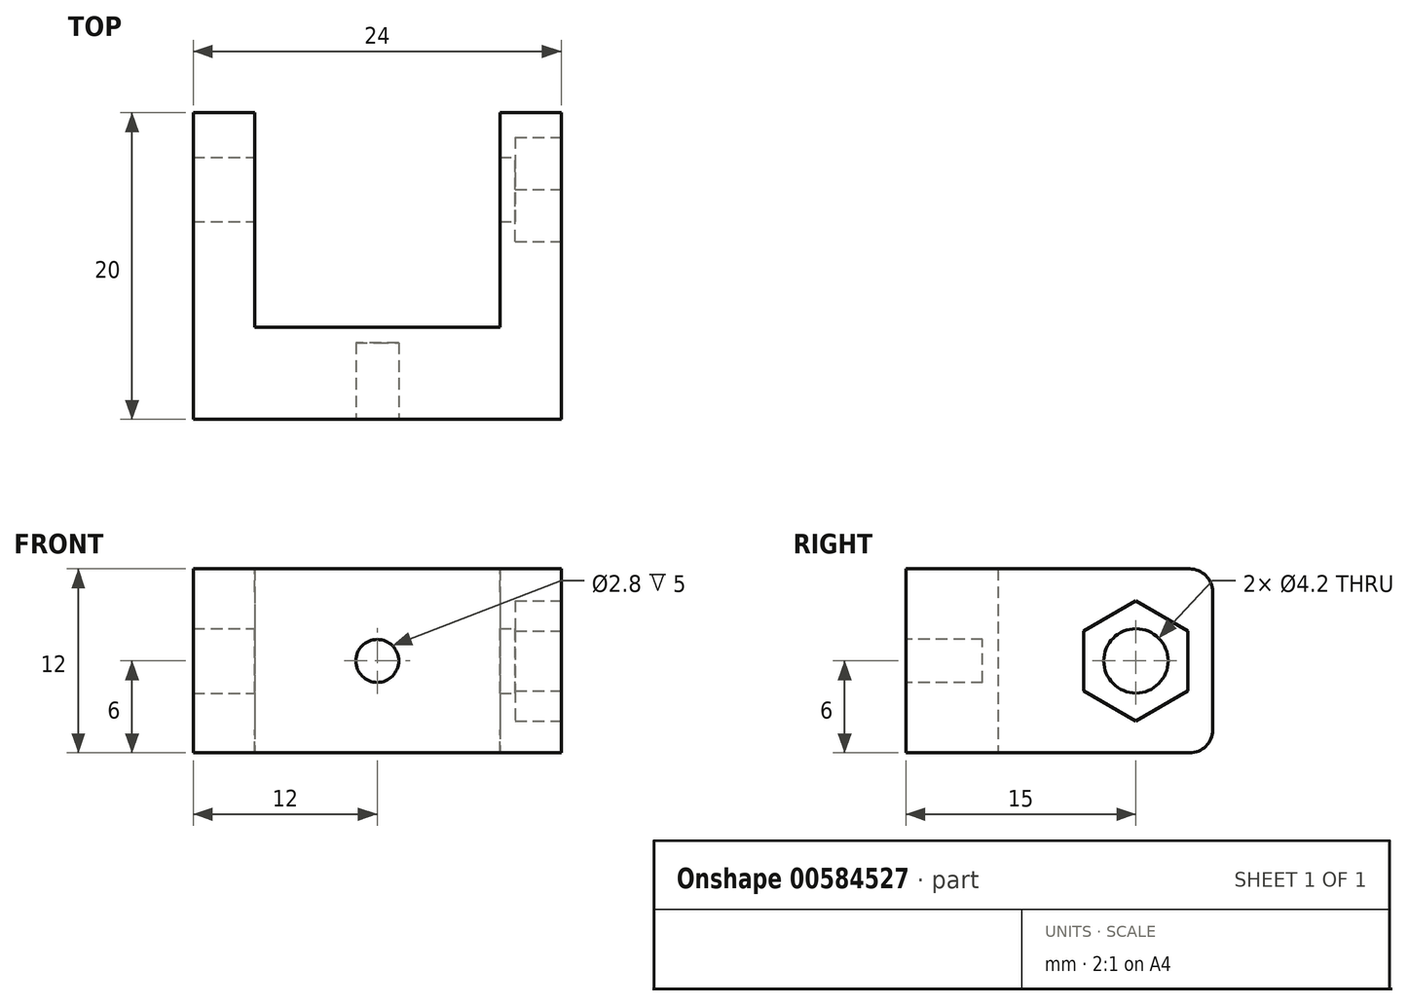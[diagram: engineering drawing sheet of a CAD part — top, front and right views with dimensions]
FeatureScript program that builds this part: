
annotation { "Feature Type Name" : "Feature", "Feature Type Description" : "" }
export const myFeature = defineFeature(function(context is Context, id is Id, definition is map)
    precondition{}
    {
        {
            var Q0;
            Q0=qCreatedBy(makeId("Top.planeOp"),FACE);
            var sketch = newSketch(context, id + "F0", { "sketchPlane" : qUnion([Q0])});
            skLineSegment(sketch, "E0.bottom", {"start": v(12, 10) * mm, "end": v(8, 10) * mm});
            skLineSegment(sketch, "E0.top", {"start": v(12, -10) * mm, "end": v(-12, -10) * mm});
            skLineSegment(sketch, "E0.left", {"start": v(12, 10) * mm, "end": v(12, -10) * mm});
            skLineSegment(sketch, "E0.right", {"start": v(-12, 10) * mm, "end": v(-12, -10) * mm});
            skPoint(sketch, "E0.middle", {"position": v(0, 0) * mm});
            skLineSegment(sketch, "E1", {"start": v(-8, 10) * mm, "end": v(-8, -4) * mm});
            skLineSegment(sketch, "E2", {"start": v(-8, -4) * mm, "end": v(0, -4) * mm});
            skLineSegment(sketch, "E3.MirrorCS", {"start": v(8, 10) * mm, "end": v(8, -4) * mm});
            skLineSegment(sketch, "E4.MirrorCS", {"start": v(8, -4) * mm, "end": v(0, -4) * mm});
            skLineSegment(sketch, "E5.trimOffspring", {"start": v(-8, 10) * mm, "end": v(-12, 10) * mm});
            skSolve(sketch);
        }
        {
            var Q0;
            Q0 = qSketchRegion(id + "F0", true);
            extrude(context, id + "F1", {"entities" : qUnion([Q0]), "endBound" : BoundingType.SYMMETRIC, "depth" : 12 * mm, "offsetDistance" : 25 * mm});
        }
        {
            var Q0;
            Q0=qCreatedBy(makeId("Right.planeOp"),FACE);
            var sketch = newSketch(context, id + "F2", { "sketchPlane" : qUnion([Q0])});
            skLineSegment(sketch, "E6", {"start": v(0, 0) * mm, "end": v(17.34, 0) * mm, "construction": true});
            skCircle(sketch, "E7", {"center": v(5, 0) * mm, "radius": 2.1 * mm});
            skSolve(sketch);
        }
        {
            var Q0;
            Q0 = qSketchRegion(id + "F2", true);
            extrude(context, id + "F3", {"entities" : qUnion([Q0]), "operationType" : NewBodyOperationType.REMOVE, "endBound" : BoundingType.SYMMETRIC, "oppositeDirection" : true, "depth" : 50 * mm, "offsetDistance" : 25 * mm});
        }
        {
            var Q0;
            Q0=makeQuery(id+"F1.opExtrude","SWEPT_FACE",FACE,{"disambiguationData":[OSD([sQuery(id+"F0.wireOp",EDGE,"E0.left")])]});
            cPlane(context, id + "F4", {"entities" : qUnion([Q0]), "cplaneType" : CPlaneType.OFFSET, "offset" : 0 * mm, "width" : 150 * mm, "height" : 150 * mm});
        }
        {
            var Q0;
            Q0=qCreatedBy(id+"F4.planeOp",FACE);
            var sketch = newSketch(context, id + "F5", { "sketchPlane" : qUnion([Q0])});
            skCircle(sketch, "E8.cCircle", {"center": v(5, 0) * mm, "radius": 3.4 * mm, "construction": true});
            skLineSegment(sketch, "E8.0", {"start": v(8.4, -1.96) * mm, "end": v(5, -3.93) * mm});
            skLineSegment(sketch, "E8.1", {"start": v(5, -3.93) * mm, "end": v(1.6, -1.96) * mm});
            skLineSegment(sketch, "E8.2", {"start": v(1.6, -1.96) * mm, "end": v(1.6, 1.96) * mm});
            skLineSegment(sketch, "E8.3", {"start": v(1.6, 1.96) * mm, "end": v(5, 3.93) * mm});
            skLineSegment(sketch, "E8.4", {"start": v(5, 3.93) * mm, "end": v(8.4, 1.96) * mm});
            skLineSegment(sketch, "E8.5", {"start": v(8.4, 1.96) * mm, "end": v(8.4, -1.96) * mm});
            skPoint(sketch, "E8.0.midPoint", {"position": v(6.7, -2.94) * mm});
            skSolve(sketch);
        }
        {
            var Q0;
            Q0 = qSketchRegion(id + "F5", true);
            extrude(context, id + "F6", {"entities" : qUnion([Q0]), "operationType" : NewBodyOperationType.REMOVE, "oppositeDirection" : true, "depth" : 3 * mm, "offsetDistance" : 25 * mm});
        }
        {
            var Q0;
            Q0=makeQuery(id+"F1.opExtrude","CAP_EDGE",EDGE,{"disambiguationData":[OSD([sQuery(id+"F0.wireOp",EDGE,"E0.bottom")])],"isStart":true});
            var Q1;
            Q1=makeQuery(id+"F1.opExtrude","CAP_EDGE",EDGE,{"disambiguationData":[OSD([sQuery(id+"F0.wireOp",EDGE,"E0.bottom")])],"isStart":false});
            var Q2;
            Q2=makeQuery(id+"F1.opExtrude","CAP_EDGE",EDGE,{"disambiguationData":[OSD([sQuery(id+"F0.wireOp",EDGE,"E5.trimOffspring")])],"isStart":true});
            var Q3;
            Q3=makeQuery(id+"F1.opExtrude","CAP_EDGE",EDGE,{"disambiguationData":[OSD([sQuery(id+"F0.wireOp",EDGE,"E5.trimOffspring")])],"isStart":false});
            fillet(context, id + "F7", {"entities" : qUnion([Q0, Q1, Q2, Q3]), "tangentPropagation" : true, "radius" : 1.5 * mm, "defaultsChanged" : true, "vertexSettings" : [], "allowEdgeOverflow" : false});
        }
        {
            var Q0;
            Q0=makeQuery(id+"F1.opExtrude","SWEPT_FACE",FACE,{"disambiguationData":[OSD([sQuery(id+"F0.wireOp",EDGE,"E0.top")])]});
            cPlane(context, id + "F8", {"entities" : qUnion([Q0]), "cplaneType" : CPlaneType.OFFSET, "offset" : 0 * mm, "width" : 150 * mm, "height" : 150 * mm});
        }
        {
            var Q0;
            Q0=qCreatedBy(id+"F8.planeOp",FACE);
            var sketch = newSketch(context, id + "F9", { "sketchPlane" : qUnion([Q0])});
            skCircle(sketch, "E9", {"center": v(0, 0) * mm, "radius": 1.4 * mm});
            skSolve(sketch);
        }
        {
            var Q0;
            Q0=makeQuery(id+"F9.imprint","IMPRINT",FACE,{"disambiguationData":[TD([[makeQuery(id+"F9.imprint","IMPRINT",EDGE,{"derivedFrom":sQuery(id+"F9.wireOp",EDGE,"E9")}),1.0]])]});
            extrude(context, id + "F10", {"entities" : qUnion([Q0]), "operationType" : NewBodyOperationType.REMOVE, "oppositeDirection" : true, "depth" : 5 * mm, "offsetDistance" : 25 * mm});
        }
    });
